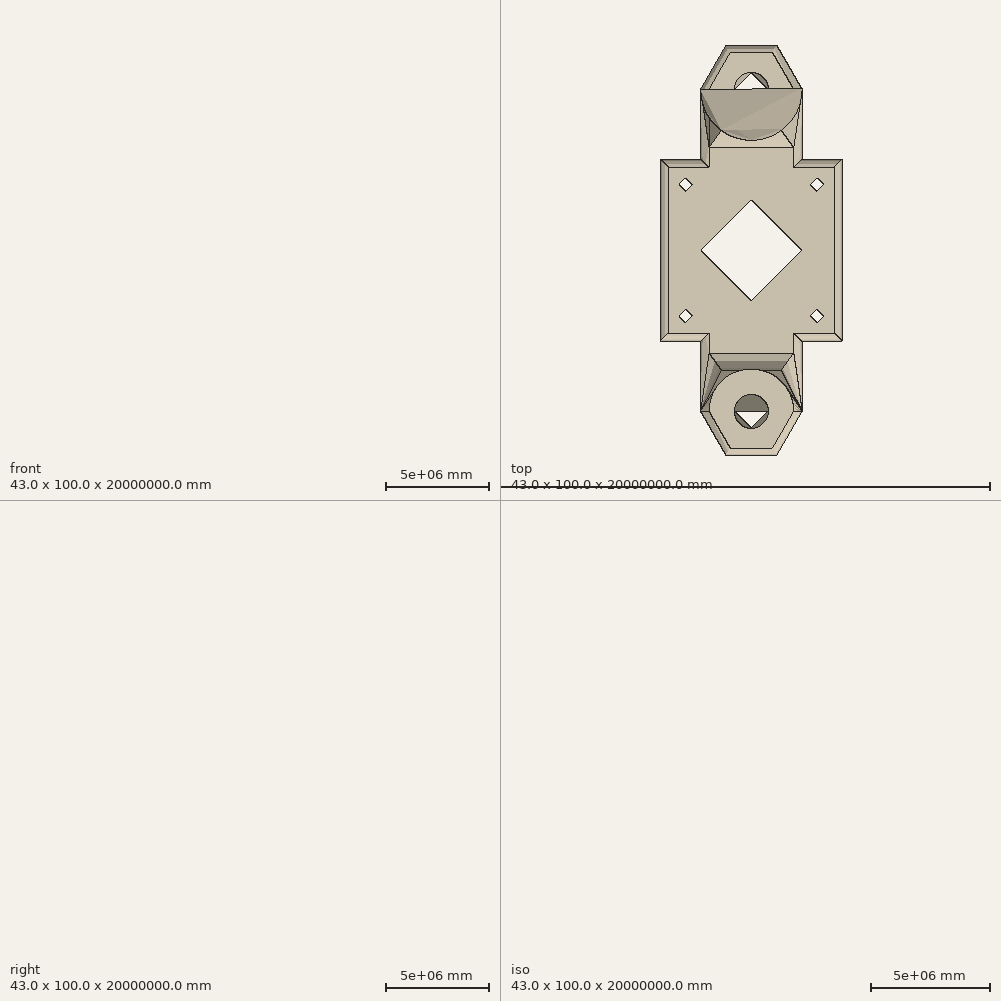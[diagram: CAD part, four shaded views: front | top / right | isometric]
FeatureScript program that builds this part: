
annotation { "Feature Type Name" : "Feature", "Feature Type Description" : "" }
export const myFeature = defineFeature(function(context is Context, id is Id, definition is map)
    precondition{}
    {
        {
            var Q0;
            Q0=qCreatedBy(makeId("Top.planeOp"),FACE);
            var sketch = newSketch(context, id + "F0", { "sketchPlane" : qUnion([Q0])});
            skCircle(sketch, "E0", {"center": v(0, -38) * mm, "radius": 4 * mm});
            skCircle(sketch, "E1", {"center": v(0, 38) * mm, "radius": 4 * mm});
            skCircle(sketch, "E2", {"center": v(0, 0) * mm, "radius": 12 * mm});
            skLineSegment(sketch, "E3", {"start": v(-12, -38) * mm, "end": v(-12, -21.5) * mm});
            skLineSegment(sketch, "E4", {"start": v(12, -38) * mm, "end": v(12, -21.5) * mm});
            skCircle(sketch, "E5", {"center": v(15.5, 15.5) * mm, "radius": 1.6 * mm});
            skCircle(sketch, "E6", {"center": v(15.5, -15.5) * mm, "radius": 1.6 * mm});
            skCircle(sketch, "E7", {"center": v(-15.5, -15.5) * mm, "radius": 1.6 * mm});
            skCircle(sketch, "E8", {"center": v(-15.5, 15.5) * mm, "radius": 1.6 * mm});
            skLineSegment(sketch, "E9", {"start": v(-21.5, 21.5) * mm, "end": v(-12, 21.5) * mm});
            skLineSegment(sketch, "E10", {"start": v(21.5, 21.5) * mm, "end": v(21.5, -21.5) * mm});
            skLineSegment(sketch, "E11", {"start": v(21.5, -21.5) * mm, "end": v(12, -21.5) * mm});
            skLineSegment(sketch, "E12", {"start": v(-21.5, -21.5) * mm, "end": v(-21.5, 21.5) * mm});
            skLineSegment(sketch, "E13", {"start": v(12, 21.5) * mm, "end": v(12, 38) * mm});
            skLineSegment(sketch, "E14", {"start": v(-12, 21.5) * mm, "end": v(-12, 38) * mm});
            skLineSegment(sketch, "E15", {"start": v(12, 21.5) * mm, "end": v(21.5, 21.5) * mm});
            skLineSegment(sketch, "E16", {"start": v(-12, -21.5) * mm, "end": v(-21.5, -21.5) * mm});
            skCircle(sketch, "E17", {"center": v(0, -38) * mm, "radius": 12 * mm});
            skCircle(sketch, "E18", {"center": v(0, 38) * mm, "radius": 12 * mm});
            skSolve(sketch);
        }
        {
            var Q0;
            Q0=makeQuery(id+"F0.imprint","IMPRINT",FACE,{"disambiguationData":[TD([[makeQuery(id+"F0.imprint","IMPRINT",EDGE,{"derivedFrom":sQuery(id+"F0.wireOp",EDGE,"E2")}),-1.0]])]});
            extrude(context, id + "F1", {"entities" : qUnion([Q0]), "depth" : 7 * mm});
        }
        {
            var Q0;
            Q0=makeQuery(id+"F0.imprint","IMPRINT",FACE,{"disambiguationData":[TD([[makeQuery(id+"F0.imprint","IMPRINT",EDGE,{"derivedFrom":sQuery(id+"F0.wireOp",EDGE,"E0")}),-1.0]])]});
            var Q1;
            Q1=makeQuery(id+"F0.imprint","IMPRINT",FACE,{"disambiguationData":[TD([[makeQuery(id+"F0.imprint","IMPRINT",EDGE,{"derivedFrom":sQuery(id+"F0.wireOp",EDGE,"E1")}),-1.0]])]});
            extrude(context, id + "F2", {"entities" : qUnion([Q0, Q1]), "operationType" : NewBodyOperationType.ADD, "depth" : 24 * mm});
        }
        {
            var Q0;
            Q0=makeQuery(id+"F2.opExtrude","CAP_EDGE",EDGE,{"disambiguationData":[OSD([sQuery(id+"F0.wireOp",EDGE,"E17")])],"isStart":false});
            var Q1;
            Q1=makeQuery(id+"F2.opExtrude","CAP_EDGE",EDGE,{"disambiguationData":[OSD([sQuery(id+"F0.wireOp",EDGE,"E18")])],"isStart":false});
            var Q2;
            Q2=makeQuery(id+"F2.opExtrude","CAP_EDGE",EDGE,{"disambiguationData":[OSD([sQuery(id+"F0.wireOp",EDGE,"E18")])],"isStart":true});
            var Q3;
            Q3=makeQuery(id+"F2.opExtrude","CAP_EDGE",EDGE,{"disambiguationData":[OSD([sQuery(id+"F0.wireOp",EDGE,"E17")])],"isStart":true});
            var Q4;
            Q4=makeQuery(id+"F1.opExtrude","CAP_EDGE",EDGE,{"disambiguationData":[OSD([sQuery(id+"F0.wireOp",EDGE,"E4")])],"isStart":false});
            var Q5;
            Q5=makeQuery(id+"F1.opExtrude","CAP_EDGE",EDGE,{"disambiguationData":[OSD([sQuery(id+"F0.wireOp",EDGE,"E11")])],"isStart":false});
            var Q6;
            Q6=makeQuery(id+"F1.opExtrude","CAP_EDGE",EDGE,{"disambiguationData":[OSD([sQuery(id+"F0.wireOp",EDGE,"E10")])],"isStart":false});
            var Q7;
            Q7=makeQuery(id+"F1.opExtrude","CAP_EDGE",EDGE,{"disambiguationData":[OSD([sQuery(id+"F0.wireOp",EDGE,"E15")])],"isStart":false});
            var Q8;
            Q8=makeQuery(id+"F1.opExtrude","CAP_EDGE",EDGE,{"disambiguationData":[OSD([sQuery(id+"F0.wireOp",EDGE,"E13")])],"isStart":false});
            var Q9;
            Q9=makeQuery(id+"F1.opExtrude","CAP_EDGE",EDGE,{"disambiguationData":[OSD([sQuery(id+"F0.wireOp",EDGE,"E14")])],"isStart":false});
            var Q10;
            Q10=makeQuery(id+"F1.opExtrude","CAP_EDGE",EDGE,{"disambiguationData":[OSD([sQuery(id+"F0.wireOp",EDGE,"E9")])],"isStart":false});
            var Q11;
            Q11=makeQuery(id+"F1.opExtrude","CAP_EDGE",EDGE,{"disambiguationData":[OSD([sQuery(id+"F0.wireOp",EDGE,"E12")])],"isStart":false});
            var Q12;
            Q12=makeQuery(id+"F1.opExtrude","CAP_EDGE",EDGE,{"disambiguationData":[OSD([sQuery(id+"F0.wireOp",EDGE,"E16")])],"isStart":false});
            var Q13;
            Q13=makeQuery(id+"F1.opExtrude","CAP_EDGE",EDGE,{"disambiguationData":[OSD([sQuery(id+"F0.wireOp",EDGE,"E3")])],"isStart":false});
            fillet(context, id + "F3", {"entities" : qUnion([Q0, Q1, Q2, Q3, Q4, Q5, Q6, Q7, Q8, Q9, Q10, Q11, Q12, Q13]), "radius" : 2 * mm, "tangentPropagation" : true, "allowEdgeOverflow" : false});
        }
        {
            var Q0;
            Q0=makeQuery(id+"F1.opExtrude","CAP_EDGE",EDGE,{"disambiguationData":[OSD([sQuery(id+"F0.wireOp",EDGE,"E17")])],"isStart":false});
            var Q1;
            Q1=makeQuery(id+"F3.opFillet","BLEND_EDGE",EDGE,{"blendedFrom":[makeQuery(id+"F1.opExtrude","CAP_EDGE",EDGE,{"disambiguationData":[OSD([sQuery(id+"F0.wireOp",EDGE,"E4")])],"isStart":false}),makeQuery(id+"F2.opExtrude","SWEPT_FACE",FACE,{"disambiguationData":[OSD([sQuery(id+"F0.wireOp",EDGE,"E17")])]})],"blendedInto":[makeQuery(id+"F2.opExtrude","SWEPT_FACE",FACE,{"disambiguationData":[OSD([sQuery(id+"F0.wireOp",EDGE,"E17")])]})]});
            var Q2;
            Q2=makeQuery(id+"F3.opFillet","BLEND_EDGE",EDGE,{"blendedFrom":[makeQuery(id+"F1.opExtrude","CAP_EDGE",EDGE,{"disambiguationData":[OSD([sQuery(id+"F0.wireOp",EDGE,"E13")])],"isStart":false}),makeQuery(id+"F2.opExtrude","SWEPT_FACE",FACE,{"disambiguationData":[OSD([sQuery(id+"F0.wireOp",EDGE,"E18")])]})],"blendedInto":[makeQuery(id+"F2.opExtrude","SWEPT_FACE",FACE,{"disambiguationData":[OSD([sQuery(id+"F0.wireOp",EDGE,"E18")])]})]});
            var Q3;
            Q3=makeQuery(id+"F1.opExtrude","CAP_EDGE",EDGE,{"disambiguationData":[OSD([sQuery(id+"F0.wireOp",EDGE,"E18")])],"isStart":false});
            var Q4;
            Q4=makeQuery(id+"F3.opFillet","BLEND_EDGE",EDGE,{"blendedFrom":[makeQuery(id+"F1.opExtrude","CAP_EDGE",EDGE,{"disambiguationData":[OSD([sQuery(id+"F0.wireOp",EDGE,"E14")])],"isStart":false}),makeQuery(id+"F2.opExtrude","SWEPT_FACE",FACE,{"disambiguationData":[OSD([sQuery(id+"F0.wireOp",EDGE,"E18")])]})],"blendedInto":[makeQuery(id+"F2.opExtrude","SWEPT_FACE",FACE,{"disambiguationData":[OSD([sQuery(id+"F0.wireOp",EDGE,"E18")])]})]});
            var Q5;
            Q5=makeQuery(id+"F3.opFillet","BLEND_EDGE",EDGE,{"blendedFrom":[makeQuery(id+"F1.opExtrude","CAP_EDGE",EDGE,{"disambiguationData":[OSD([sQuery(id+"F0.wireOp",EDGE,"E3")])],"isStart":false}),makeQuery(id+"F2.opExtrude","SWEPT_FACE",FACE,{"disambiguationData":[OSD([sQuery(id+"F0.wireOp",EDGE,"E17")])]})],"blendedInto":[makeQuery(id+"F2.opExtrude","SWEPT_FACE",FACE,{"disambiguationData":[OSD([sQuery(id+"F0.wireOp",EDGE,"E17")])]})]});
            fillet(context, id + "F4", {"entities" : qUnion([Q0, Q1, Q2, Q3, Q4, Q5]), "radius" : 5 * mm, "tangentPropagation" : true, "allowEdgeOverflow" : false});
        }
    });
